FCSTD DOCUMENT  (FreeCAD 0.19R24291 (Git))
Label: v1-250-frame
License: Other
LicenseURL: GPL3
objects: Part::FeaturePython×84, Part::Feature×55, App::Part×7
note: 139 computed .brp shape members not serialized (recipe doc carries the construction recipe); baked Part::Feature solids carry a one-line shape summary decoded from their .brp

FEATURE [Part::Feature] Extrude002002003002002002002  label="380mm-tap"
  Placement = pos=(-190,0,15) rot=(0,1,0;1.5708rad)
  shape: bbox 380 x 30 x 30 mm, 95 faces (baked)
FEATURE [Part::Feature] Extrude002002003002002002007  label="380mm-tap001"
  Placement = pos=(-190,390,15) rot=(0,1,0;1.5708rad)
  shape: bbox 380 x 30 x 30 mm, 95 faces (baked)
FEATURE [Part::Feature] Extrude002002003002002002010  label="380mm-tap002"
  Placement = pos=(-190,390,535) rot=(0,1,0;1.5708rad)
  shape: bbox 380 x 30 x 30 mm, 95 faces (baked)
FEATURE [Part::Feature] Extrude002002003002002002011  label="360mm-tap"
  Placement = pos=(-205,15,535) rot=(-1,0,0;1.5708rad)
  shape: bbox 30 x 360 x 30 mm, 95 faces (baked)
FEATURE [Part::Feature] Extrude002002003002002002012  label="360mm-tap001"
  Placement = pos=(205,15,535) rot=(-1,0,0;1.5708rad)
  shape: bbox 30 x 360 x 30 mm, 95 faces (baked)
FEATURE [Part::Feature] Extrude002002003002002002013  label="380mm-tap003"
  Placement = pos=(-190,0,535) rot=(0,1,0;1.5708rad)
  shape: bbox 380 x 30 x 30 mm, 95 faces (baked)
FEATURE [Part::Feature] Extrude002002003002002002015  label="330mm-tap"
  Placement = pos=(-205,250,30) rot=(0,0,1;0rad)
  shape: bbox 30 x 30 x 330 mm, 95 faces (baked)
FEATURE [Part::Feature] Extrude002002003002002002016  label="330mm-tap001"
  Placement = pos=(205,140,30) rot=(0,0,1;0rad)
  shape: bbox 30 x 30 x 330 mm, 95 faces (baked)
FEATURE [Part::Feature] Extrude002002003002002002019  label="380mm-tap004"
  Placement = pos=(-190,390,340) rot=(0,1,0;1.5708rad)
  shape: bbox 380 x 30 x 30 mm, 95 faces (baked)
FEATURE [Part::Feature] Cut001  label="550mm-drint--tap-front-vetical"
  Placement = pos=(-205,0,0) rot=(0,0,1;0rad)
  shape: bbox 30 x 30 x 550 mm, 167 faces (baked)
FEATURE [Part::Feature] Cut002  label="550mm-drint--tap-front-vetical001"
  Placement = pos=(205,0,0) rot=(0,0,1;0rad)
  shape: bbox 30 x 30 x 550 mm, 167 faces (baked)
FEATURE [Part::Feature] Cut001001  label="550mm-drill-tap-back-vertical"
  Placement = pos=(205,390,0) rot=(0,0,1;0rad)
  shape: bbox 30 x 30 x 550 mm, 181 faces (baked)
FEATURE [Part::Feature] Cut001002  label="550mm-drill-tap-back-vertical001"
  Placement = pos=(-205,390,0) rot=(0,0,1;0rad)
  shape: bbox 30 x 30 x 550 mm, 181 faces (baked)
FEATURE [Part::Feature] Cut001003  label="330-drill-vertical"
  Placement = pos=(-205,30,30) rot=(0,0,1;0rad)
  shape: bbox 30 x 30 x 330 mm, 137 faces (baked)
FEATURE [Part::Feature] Cut001004  label="360mm-drill-tap-left-horizontal"
  Placement = pos=(-205,15,15) rot=(-1,0,0;1.5708rad)
  shape: bbox 30 x 360 x 30 mm, 109 faces (baked)
FEATURE [Part::Feature] Cut001005  label="360mm-drill-tap-right-horizontal"
  Placement = pos=(205,15,15) rot=(-1,0,0;1.5708rad)
  shape: bbox 30 x 360 x 30 mm, 109 faces (baked)
FEATURE [Part::Feature] Cut001006  label="360mm-drill-tap-left-horizontal001"
  Placement = pos=(-205,15,375) rot=(-1,0,0;1.5708rad)
  shape: bbox 30 x 360 x 30 mm, 109 faces (baked)
FEATURE [Part::Feature] Cut001007  label="360mm-drill-tap-right-horizontal001"
  Placement = pos=(205,15,375) rot=(-1,0,0;1.5708rad)
  shape: bbox 30 x 360 x 30 mm, 109 faces (baked)
FEATURE [App::Part] Part  label="250-frame"
  Group = -> [Extrude002002003002002002002,Extrude002002003002002002007,Extrude002002003002002002010,Extrude002002003002002002011,Extrude002002003002002002012,Extrude002002003002002002013,Extrude002002003002002002015,Extrude002002003002002002016,Extrude002002003002002002019,Cut001,Cut002,Cut001001,Cut001002,Cut001003,Cut001004,Cut001005,Cut001006,Cut001007]
  Origin = -> Origin
FEATURE [Part::FeaturePython] Screw039  label="M3x6-Screw048"  # Fasteners workbench fastener (typed FeaturePython)
  Placement = pos=(111,-6.5,2.5) rot=(0,0,1;0rad)
  baseObject = -> Chamfer004001 [Edge92]
  diameter = 1
  invert = false
  length = 0
  lengthCustom = 6
  matchOuter = true
  offset = 0
  thread = false
  type = 40
FEATURE [Part::Feature] Pocket003005  label="panel-mounter_D001"
  Placement = pos=(-179.5,-180,-10) rot=(0.57735,0.57735,0.57735;2.0944rad)
  shape: bbox 10 x 15 x 20 mm, 54 faces (baked)
FEATURE [Part::FeaturePython] Screw002  label="M6x12-Screw006"  # Fasteners workbench fastener (typed FeaturePython)
  Placement = pos=(55,175,-10) rot=(1,0,0;1.5708rad)
  baseObject = -> Chamfer003004004 [Edge49]
  diameter = 4
  invert = true
  length = 1
  lengthCustom = 12
  matchOuter = true
  offset = 0
  thread = false
  type = 40
FEATURE [Part::FeaturePython] HeatSet030  label="M3x4-HeatSet039"  # WARN: FeaturePython — macro-defined, semantics opaque (R4)
  Placement = pos=(-62,-7,5) rot=(0,0,1;0rad)
  diameter = 2
  invert = false
  offset = 0
FEATURE [Part::FeaturePython] HeatSet031  label="M3x4-HeatSet040"  # WARN: FeaturePython — macro-defined, semantics opaque (R4)
  Placement = pos=(-70,-144,5) rot=(0,0,1;0rad)
  diameter = 2
  invert = false
  offset = 0
FEATURE [Part::FeaturePython] HeatSet032  label="M3x4-HeatSet041"  # WARN: FeaturePython — macro-defined, semantics opaque (R4)
  Placement = pos=(-62,7,5) rot=(0,0,1;0rad)
  diameter = 2
  invert = false
  offset = 0
FEATURE [Part::FeaturePython] HeatSet033  label="M3x4-HeatSet042"  # WARN: FeaturePython — macro-defined, semantics opaque (R4)
  Placement = pos=(62,-7,5) rot=(0,0,1;0rad)
  diameter = 2
  invert = false
  offset = 0
FEATURE [Part::FeaturePython] HeatSet034  label="M3x4-HeatSet043"  # WARN: FeaturePython — macro-defined, semantics opaque (R4)
  Placement = pos=(70,-144,5) rot=(0,0,1;0rad)
  diameter = 2
  invert = false
  offset = 0
FEATURE [Part::FeaturePython] HeatSet035  label="M3x4-HeatSet044"  # WARN: FeaturePython — macro-defined, semantics opaque (R4)
  Placement = pos=(62,7,5) rot=(0,0,1;0rad)
  diameter = 2
  invert = false
  offset = 0
FEATURE [Part::FeaturePython] Screw020  label="M3x6-Screw029"  # Fasteners workbench fastener (typed FeaturePython)
  Placement = pos=(185,50.94,2.5) rot=(0,0,1;0rad)
  diameter = 1
  invert = false
  length = 0
  lengthCustom = 6
  matchOuter = true
  offset = 0
  thread = false
  type = 40
FEATURE [Part::FeaturePython] Screw021  label="M3x6-Screw030"  # Fasteners workbench fastener (typed FeaturePython)
  Placement = pos=(184,175,2.5) rot=(0,0,1;0rad)
  diameter = 1
  invert = false
  length = 0
  lengthCustom = 6
  matchOuter = true
  offset = 0
  thread = false
  type = 40
FEATURE [Part::FeaturePython] HeatSet011  label="M3x4-HeatSet013"  # WARN: FeaturePython — macro-defined, semantics opaque (R4)
  Placement = pos=(-185,-59.4,1.2e-14) rot=(0,0,1;0rad)
  baseObject = -> Pocket003020 [Edge44]
  diameter = 2
  invert = false
  offset = 0
FEATURE [Part::FeaturePython] HeatSet012  label="M3x4-HeatSet012"  # WARN: FeaturePython — macro-defined, semantics opaque (R4)
  Placement = pos=(-174.5,-175,3.91e-14) rot=(0,0,1;0rad)
  baseObject = -> Pocket003005 [Edge44]
  diameter = 2
  invert = false
  offset = 0
FEATURE [Part::FeaturePython] HeatSet013  label="M3x4-HeatSet011"  # WARN: FeaturePython — macro-defined, semantics opaque (R4)
  Placement = pos=(-82,-175,3.91e-14) rot=(0,0,1;0rad)
  baseObject = -> Pocket003006 [Edge44]
  diameter = 2
  invert = false
  offset = 0
FEATURE [Part::FeaturePython] HeatSet014  label="M3x4-HeatSet027"  # WARN: FeaturePython — macro-defined, semantics opaque (R4)
  Placement = pos=(-28,-175,3.91e-14) rot=(0,0,1;0rad)
  baseObject = -> Pocket003007 [Edge44]
  diameter = 2
  invert = false
  offset = 0
FEATURE [Part::FeaturePython] HeatSet015  label="M3x4-HeatSet020"  # WARN: FeaturePython — macro-defined, semantics opaque (R4)
  Placement = pos=(28,-175,3.91e-14) rot=(0,0,1;0rad)
  baseObject = -> Pocket003008 [Edge44]
  diameter = 2
  invert = false
  offset = 0
FEATURE [Part::FeaturePython] HeatSet016  label="M3x4-HeatSet021"  # WARN: FeaturePython — macro-defined, semantics opaque (R4)
  Placement = pos=(82,-175,3.91e-14) rot=(0,0,1;0rad)
  baseObject = -> Pocket003009 [Edge44]
  diameter = 2
  invert = false
  offset = 0
FEATURE [Part::Feature] Chamfer003004005  label="bottom-din-holder003"
  Placement = pos=(-55,165,-25) rot=(0,0,1;0rad)
  shape: bbox 40 x 31 x 21 mm, 75 faces (baked)
FEATURE [Part::Feature] Pocket003021  label="panel-mounter_R001"
  Placement = pos=(190,45.9,-10) rot=(0,0.707107,0.707107;3.14159rad)
  shape: bbox 15 x 10 x 20 mm, 54 faces (baked)
FEATURE [Part::Feature] Pocket003014  label="panel-mounter_U004"
  Placement = pos=(33,180,-10) rot=(0.57735,-0.57735,-0.57735;2.0944rad)
  shape: bbox 10 x 15 x 20 mm, 54 faces (baked)
FEATURE [Part::FeaturePython] Nut002  label="M4-Nut005"  # Fasteners workbench fastener (typed FeaturePython)
  Placement = pos=(55,161,-18) rot=(1,0,0;3.14159rad)
  baseObject = -> Chamfer003004004 [Edge141]
  diameter = 6
  invert = true
  matchOuter = true
  offset = 0
  thread = false
  type = 7
FEATURE [Part::FeaturePython] Nut003  label="M4-Nut006"  # Fasteners workbench fastener (typed FeaturePython)
  Placement = pos=(-55,161,-18) rot=(1,0,0;3.14159rad)
  baseObject = -> Chamfer003004005 [Edge141]
  diameter = 6
  invert = true
  matchOuter = true
  offset = 0
  thread = false
  type = 7
FEATURE [Part::FeaturePython] Screw012  label="M3x6-Screw004"  # Fasteners workbench fastener (typed FeaturePython)
  Placement = pos=(62,7,8) rot=(0,0,1;0rad)
  baseObject = -> Cut002015026005020007004002 [Edge40]
  diameter = 1
  invert = false
  length = 0
  lengthCustom = 6
  matchOuter = true
  offset = 0
  thread = false
  type = 40
FEATURE [Part::FeaturePython] Screw013  label="M3x6-Screw005"  # Fasteners workbench fastener (typed FeaturePython)
  Placement = pos=(62,-7,8) rot=(0,0,1;0rad)
  baseObject = -> Cut002015026005020007004002 [Edge39]
  diameter = 1
  invert = false
  length = 0
  lengthCustom = 6
  matchOuter = true
  offset = 0
  thread = false
  type = 40
FEATURE [Part::FeaturePython] Screw014  label="M3x6-Screw006"  # Fasteners workbench fastener (typed FeaturePython)
  Placement = pos=(48,-7,8) rot=(0,0,1;0rad)
  baseObject = -> Cut002015026005020007004002 [Edge41]
  diameter = 1
  invert = false
  length = 0
  lengthCustom = 6
  matchOuter = true
  offset = 0
  thread = false
  type = 40
FEATURE [Part::FeaturePython] Screw  label="M6x12-Screw004"  # Fasteners workbench fastener (typed FeaturePython)
  Placement = pos=(-55,-175,-10) rot=(-1,0,0;1.5708rad)
  baseObject = -> Chamfer003004002 [Edge49]
  diameter = 4
  invert = true
  length = 1
  lengthCustom = 12
  matchOuter = true
  offset = 0
  thread = false
  type = 40
FEATURE [Part::FeaturePython] Screw015  label="M3x6-Screw007"  # Fasteners workbench fastener (typed FeaturePython)
  Placement = pos=(48,7,8) rot=(0,0,1;0rad)
  baseObject = -> Cut002015026005020007004002 [Edge42]
  diameter = 1
  invert = false
  length = 0
  lengthCustom = 6
  matchOuter = true
  offset = 0
  thread = false
  type = 40
FEATURE [Part::FeaturePython] Screw016  label="M3x6-Screw008"  # Fasteners workbench fastener (typed FeaturePython)
  Placement = pos=(-48,7,8) rot=(0,0,1;0rad)
  baseObject = -> Cut002015026005020007004001 [Edge40]
  diameter = 1
  invert = false
  length = 0
  lengthCustom = 6
  matchOuter = true
  offset = 0
  thread = false
  type = 40
FEATURE [Part::FeaturePython] Screw017  label="M3x6-Screw009"  # Fasteners workbench fastener (typed FeaturePython)
  Placement = pos=(-48,-7,8) rot=(0,0,1;0rad)
  baseObject = -> Cut002015026005020007004001 [Edge39]
  diameter = 1
  invert = false
  length = 0
  lengthCustom = 6
  matchOuter = true
  offset = 0
  thread = false
  type = 40
FEATURE [Part::FeaturePython] Screw018  label="M3x6-Screw010"  # Fasteners workbench fastener (typed FeaturePython)
  Placement = pos=(-62,-7,8) rot=(0,0,1;0rad)
  baseObject = -> Cut002015026005020007004001 [Edge41]
  diameter = 1
  invert = false
  length = 0
  lengthCustom = 6
  matchOuter = true
  offset = 0
  thread = false
  type = 40
FEATURE [Part::FeaturePython] Screw019  label="M3x6-Screw011"  # Fasteners workbench fastener (typed FeaturePython)
  Placement = pos=(-62,7,8) rot=(0,0,1;0rad)
  baseObject = -> Cut002015026005020007004001 [Edge42]
  diameter = 1
  invert = false
  length = 0
  lengthCustom = 6
  matchOuter = true
  offset = 0
  thread = false
  type = 40
FEATURE [Part::Feature] Pocket003007  label="panel-mounter_D003"
  Placement = pos=(-33,-180,-10) rot=(0.57735,0.57735,0.57735;2.0944rad)
  shape: bbox 10 x 15 x 20 mm, 54 faces (baked)
FEATURE [Part::Feature] Pocket003006  label="panel-mounter_D002"
  Placement = pos=(-87,-180,-10) rot=(0.57735,0.57735,0.57735;2.0944rad)
  shape: bbox 10 x 15 x 20 mm, 54 faces (baked)
FEATURE [Part::Feature] Chamfer005007002029002004001  label="back-din-cap"
  Placement = pos=(-55,165,-25) rot=(0,0,1;0rad)
  shape: bbox 40 x 30 x 6 mm, 55 faces (baked)
FEATURE [Part::FeaturePython] Screw004  label="M4x25-Screw"  # Fasteners workbench fastener (typed FeaturePython)
  Placement = pos=(-55,161,2.5) rot=(0,0,1;0rad)
  baseObject = -> Chamfer005007002029002004001 [Edge49]
  diameter = 2
  invert = false
  length = 7
  lengthCustom = 25
  matchOuter = true
  offset = 0
  thread = false
  type = 40
FEATURE [Part::FeaturePython] HeatSet002  label="M3x4-HeatSet025"  # WARN: FeaturePython — macro-defined, semantics opaque (R4)
  Placement = pos=(184,175,1.8e-15) rot=(0,0,1;0rad)
  baseObject = -> Pocket003016 [Edge44]
  diameter = 2
  invert = false
  offset = 0
FEATURE [Part::FeaturePython] HeatSet003  label="M3x4-HeatSet026"  # WARN: FeaturePython — macro-defined, semantics opaque (R4)
  Placement = pos=(82,175,1.8e-15) rot=(0,0,1;0rad)
  baseObject = -> Pocket003015 [Edge44]
  diameter = 2
  invert = false
  offset = 0
FEATURE [Part::FeaturePython] HeatSet004  label="M3x4-HeatSet024"  # WARN: FeaturePython — macro-defined, semantics opaque (R4)
  Placement = pos=(28,175,1.8e-15) rot=(0,0,1;0rad)
  baseObject = -> Pocket003014 [Edge44]
  diameter = 2
  invert = false
  offset = 0
FEATURE [Part::FeaturePython] HeatSet005  label="M3x4-HeatSet028"  # WARN: FeaturePython — macro-defined, semantics opaque (R4)
  Placement = pos=(-28,175,1.8e-15) rot=(0,0,1;0rad)
  baseObject = -> Pocket003013 [Edge44]
  diameter = 2
  invert = false
  offset = 0
FEATURE [Part::FeaturePython] HeatSet006  label="M3x4-HeatSet018"  # WARN: FeaturePython — macro-defined, semantics opaque (R4)
  Placement = pos=(-82,175,1.8e-15) rot=(0,0,1;0rad)
  baseObject = -> Pocket003012 [Edge44]
  diameter = 2
  invert = false
  offset = 0
FEATURE [Part::FeaturePython] HeatSet007  label="M3x4-HeatSet017"  # WARN: FeaturePython — macro-defined, semantics opaque (R4)
  Placement = pos=(-184,175,1.8e-15) rot=(0,0,1;0rad)
  baseObject = -> Pocket003011 [Edge44]
  diameter = 2
  invert = false
  offset = 0
FEATURE [Part::FeaturePython] HeatSet008  label="M3x4-HeatSet016"  # WARN: FeaturePython — macro-defined, semantics opaque (R4)
  Placement = pos=(-185,32.4,-7.1e-15) rot=(0,0,1;0rad)
  baseObject = -> Pocket003017 [Edge44]
  diameter = 2
  invert = false
  offset = 0
FEATURE [Part::FeaturePython] HeatSet009  label="M3x4-HeatSet023"  # WARN: FeaturePython — macro-defined, semantics opaque (R4)
  Placement = pos=(-185,6.6,-1.8e-15) rot=(0,0,1;0rad)
  baseObject = -> Pocket003018 [Edge44]
  diameter = 2
  invert = false
  offset = 0
FEATURE [Part::FeaturePython] HeatSet010  label="M3x4-HeatSet014"  # WARN: FeaturePython — macro-defined, semantics opaque (R4)
  Placement = pos=(-185,-6.5,2e-15) rot=(0,0,1;0rad)
  baseObject = -> Pocket003019 [Edge44]
  diameter = 2
  invert = false
  offset = 0
FEATURE [Part::Feature] Cut002015026005020007004003  label="front-din-cap001"
  Placement = pos=(55,-165,0) rot=(0,0,1;0rad)
  shape: bbox 40 x 41.5 x 9 mm, 50 faces (baked)
FEATURE [Part::FeaturePython] Screw022  label="M3x6-Screw031"  # Fasteners workbench fastener (typed FeaturePython)
  Placement = pos=(82,175,2.5) rot=(0,0,1;0rad)
  diameter = 1
  invert = false
  length = 0
  lengthCustom = 6
  matchOuter = true
  offset = 0
  thread = false
  type = 40
FEATURE [Part::FeaturePython] Screw023  label="M3x6-Screw032"  # Fasteners workbench fastener (typed FeaturePython)
  Placement = pos=(28,175,2.5) rot=(0,0,1;0rad)
  diameter = 1
  invert = false
  length = 0
  lengthCustom = 6
  matchOuter = true
  offset = 0
  thread = false
  type = 40
FEATURE [Part::FeaturePython] Screw024  label="M3x6-Screw033"  # Fasteners workbench fastener (typed FeaturePython)
  Placement = pos=(-28,175,2.5) rot=(0,0,1;0rad)
  diameter = 1
  invert = false
  length = 0
  lengthCustom = 6
  matchOuter = true
  offset = 0
  thread = false
  type = 40
FEATURE [Part::FeaturePython] Screw025  label="M3x6-Screw034"  # Fasteners workbench fastener (typed FeaturePython)
  Placement = pos=(-82,175,2.5) rot=(0,0,1;0rad)
  diameter = 1
  invert = false
  length = 0
  lengthCustom = 6
  matchOuter = true
  offset = 0
  thread = false
  type = 40
FEATURE [Part::FeaturePython] Screw026  label="M3x6-Screw035"  # Fasteners workbench fastener (typed FeaturePython)
  Placement = pos=(-184,175,2.5) rot=(0,0,1;0rad)
  diameter = 1
  invert = false
  length = 0
  lengthCustom = 6
  matchOuter = true
  offset = 0
  thread = false
  type = 40
FEATURE [Part::FeaturePython] Screw027  label="M3x6-Screw036"  # Fasteners workbench fastener (typed FeaturePython)
  Placement = pos=(-185,32.5,2.5) rot=(0,0,1;0rad)
  diameter = 1
  invert = false
  length = 0
  lengthCustom = 6
  matchOuter = true
  offset = 0
  thread = false
  type = 40
FEATURE [Part::FeaturePython] Screw028  label="M3x6-Screw042"  # Fasteners workbench fastener (typed FeaturePython)
  Placement = pos=(-185,-6.5,2.5) rot=(0,0,1;0rad)
  diameter = 1
  invert = false
  length = 0
  lengthCustom = 6
  matchOuter = true
  offset = 0
  thread = false
  type = 40
FEATURE [Part::Feature] Cut002015026005020007004001  label="center-panel-connector"
  Placement = pos=(-55,0,5) rot=(0,0,1;0rad)
  shape: bbox 22 x 22 x 3 mm, 24 faces (baked)
FEATURE [Part::FeaturePython] Screw001  label="M6x12-Screw005"  # Fasteners workbench fastener (typed FeaturePython)
  Placement = pos=(55,-175,-10) rot=(-1,0,0;1.5708rad)
  baseObject = -> Chamfer003004003 [Edge49]
  diameter = 4
  invert = true
  length = 1
  lengthCustom = 12
  matchOuter = true
  offset = 0
  thread = false
  type = 40
FEATURE [Part::Feature] Pocket003008  label="panel-mounter_D004"
  Placement = pos=(23,-180,-10) rot=(0.57735,0.57735,0.57735;2.0944rad)
  shape: bbox 10 x 15 x 20 mm, 54 faces (baked)
FEATURE [Part::FeaturePython] Screw029  label="M3x6-Screw043"  # Fasteners workbench fastener (typed FeaturePython)
  Placement = pos=(-185,-59.36,2.5) rot=(0,0,1;0rad)
  diameter = 1
  invert = false
  length = 0
  lengthCustom = 6
  matchOuter = true
  offset = 0
  thread = false
  type = 40
FEATURE [Part::FeaturePython] Screw030  label="M3x6-Screw044"  # Fasteners workbench fastener (typed FeaturePython)
  Placement = pos=(-174.5,-175,2.5) rot=(0,0,1;0rad)
  diameter = 1
  invert = false
  length = 0
  lengthCustom = 6
  matchOuter = true
  offset = 0
  thread = false
  type = 40
FEATURE [Part::FeaturePython] Screw031  label="M3x6-Screw045"  # Fasteners workbench fastener (typed FeaturePython)
  Placement = pos=(-82,-175,2.5) rot=(0,0,1;0rad)
  diameter = 1
  invert = false
  length = 0
  lengthCustom = 6
  matchOuter = true
  offset = 0
  thread = false
  type = 40
FEATURE [Part::FeaturePython] Screw032  label="M3x6-Screw040"  # Fasteners workbench fastener (typed FeaturePython)
  Placement = pos=(28,-175,2.5) rot=(0,0,1;0rad)
  diameter = 1
  invert = false
  length = 0
  lengthCustom = 6
  matchOuter = true
  offset = 0
  thread = false
  type = 40
FEATURE [Part::FeaturePython] Screw033  label="M3x6-Screw041"  # Fasteners workbench fastener (typed FeaturePython)
  Placement = pos=(-28,-175,2.5) rot=(0,0,1;0rad)
  diameter = 1
  invert = false
  length = 0
  lengthCustom = 6
  matchOuter = true
  offset = 0
  thread = false
  type = 40
FEATURE [Part::FeaturePython] Screw034  label="M3x6-Screw037"  # Fasteners workbench fastener (typed FeaturePython)
  Placement = pos=(184,-175,2.5) rot=(0,0,1;0rad)
  diameter = 1
  invert = false
  length = 0
  lengthCustom = 6
  matchOuter = true
  offset = 0
  thread = false
  type = 40
FEATURE [Part::FeaturePython] Screw035  label="M3x6-Screw038"  # Fasteners workbench fastener (typed FeaturePython)
  Placement = pos=(82,-175,2.5) rot=(0,0,1;0rad)
  diameter = 1
  invert = false
  length = 0
  lengthCustom = 6
  matchOuter = true
  offset = 0
  thread = false
  type = 40
FEATURE [Part::FeaturePython] Screw036  label="M3x6-Screw039"  # Fasteners workbench fastener (typed FeaturePython)
  Placement = pos=(185,-77.5,2.5) rot=(0,0,1;0rad)
  diameter = 1
  invert = false
  length = 0
  lengthCustom = 6
  matchOuter = true
  offset = 0
  thread = false
  type = 40
FEATURE [Part::Feature] Common001003002002003003  label="din-rail-332mm002"
  Placement = pos=(93,53,20) rot=(0.707107,-0.707107,0;3.14159rad)
  shape: bbox 35 x 332 x 7.5 mm, 70 faces (baked)
FEATURE [Part::Feature] Pocket003019  label="panel-mounter_L003"
  Placement = pos=(-190,-1.5,-10) rot=(1,0,0;1.5708rad)
  shape: bbox 15 x 10 x 20 mm, 54 faces (baked)
FEATURE [Part::Feature] Pocket003017  label="panel-mounter_L001"
  Placement = pos=(-190,37.4,-10) rot=(1,0,0;1.5708rad)
  shape: bbox 15 x 10 x 20 mm, 54 faces (baked)
FEATURE [Part::FeaturePython] Screw010  label="M3x6-Screw002"  # Fasteners workbench fastener (typed FeaturePython)
  Placement = pos=(-40,-144,8) rot=(0,0,1;0rad)
  baseObject = -> Cut002015026005020007004004 [Edge45]
  diameter = 1
  invert = false
  length = 0
  lengthCustom = 6
  matchOuter = true
  offset = 0
  thread = false
  type = 40
FEATURE [Part::FeaturePython] Screw011  label="M3x6-Screw003"  # Fasteners workbench fastener (typed FeaturePython)
  Placement = pos=(-70,-144,8) rot=(0,0,1;0rad)
  baseObject = -> Cut002015026005020007004004 [Edge44]
  diameter = 1
  invert = false
  length = 0
  lengthCustom = 6
  matchOuter = true
  offset = 0
  thread = false
  type = 40
FEATURE [Part::Feature] Pocket003022  label="panel-mounter_R002"
  Placement = pos=(190,-82.5,-10) rot=(0,0.707107,0.707107;3.14159rad)
  shape: bbox 15 x 10 x 20 mm, 54 faces (baked)
FEATURE [Part::Feature] Chamfer003004004  label="bottom-din-holder002"
  Placement = pos=(55,165,-25) rot=(0,0,1;0rad)
  shape: bbox 40 x 31 x 21 mm, 75 faces (baked)
FEATURE [Part::Feature] Pocket003009  label="panel-mounter_D005"
  Placement = pos=(77,-180,-10) rot=(0.57735,0.57735,0.57735;2.0944rad)
  shape: bbox 10 x 15 x 20 mm, 54 faces (baked)
FEATURE [Part::Feature] Cut002015026005020007004002  label="center-panel-connector001"
  Placement = pos=(55,0,5) rot=(0,0,1;0rad)
  shape: bbox 22 x 22 x 3 mm, 24 faces (baked)
FEATURE [Part::Feature] Pocket003012  label="panel-mounter_U002"
  Placement = pos=(-77,180,-10) rot=(0.57735,-0.57735,-0.57735;2.0944rad)
  shape: bbox 10 x 15 x 20 mm, 54 faces (baked)
FEATURE [Part::FeaturePython] Screw003  label="M6x12-Screw"  # Fasteners workbench fastener (typed FeaturePython)
  Placement = pos=(-55,175,-10) rot=(1,0,0;1.5708rad)
  baseObject = -> Chamfer003004005 [Edge49]
  diameter = 4
  invert = true
  length = 1
  lengthCustom = 12
  matchOuter = true
  offset = 0
  thread = false
  type = 40
FEATURE [Part::FeaturePython] Nut  label="M4-Nut"  # Fasteners workbench fastener (typed FeaturePython)
  Placement = pos=(-55,-161,-18) rot=(1,0,0;3.14159rad)
  baseObject = -> Chamfer003004002 [Edge141]
  diameter = 6
  invert = true
  matchOuter = true
  offset = 0
  thread = false
  type = 7
FEATURE [Part::Feature] Pocket003011  label="panel-mounter_U001"
  Placement = pos=(-179,180,-10) rot=(0.57735,-0.57735,-0.57735;2.0944rad)
  shape: bbox 10 x 15 x 20 mm, 54 faces (baked)
FEATURE [Part::FeaturePython] HeatSet  label="M3x4-HeatSet"  # WARN: FeaturePython — macro-defined, semantics opaque (R4)
  Placement = pos=(70,170,5) rot=(0,0,1;0rad)
  baseObject = -> Chamfer005007002029002004002 [Edge114]
  diameter = 2
  invert = false
  offset = 0
FEATURE [Part::FeaturePython] HeatSet001  label="M3x4-HeatSet001"  # WARN: FeaturePython — macro-defined, semantics opaque (R4)
  Placement = pos=(40,170,5) rot=(0,0,1;0rad)
  baseObject = -> Chamfer005007002029002004002 [Edge88]
  diameter = 2
  invert = false
  offset = 0
FEATURE [Part::FeaturePython] Screw005  label="M4x25-Screw001"  # Fasteners workbench fastener (typed FeaturePython)
  Placement = pos=(55,161,2.5) rot=(0,0,1;0rad)
  baseObject = -> Chamfer005007002029002004002 [Edge49]
  diameter = 2
  invert = false
  length = 7
  lengthCustom = 25
  matchOuter = true
  offset = 0
  thread = false
  type = 40
FEATURE [Part::FeaturePython] Screw006  label="M4x25-Screw002"  # Fasteners workbench fastener (typed FeaturePython)
  Placement = pos=(55,-161,2.5) rot=(0,0,1;0rad)
  baseObject = -> Cut002015026005020007004003 [Edge118]
  diameter = 2
  invert = false
  length = 7
  lengthCustom = 25
  matchOuter = true
  offset = 0
  thread = false
  type = 40
FEATURE [Part::Feature] Chamfer005007002029002004002  label="back-din-cap001"
  Placement = pos=(55,165,-25) rot=(0,0,1;0rad)
  shape: bbox 40 x 30 x 6 mm, 55 faces (baked)
FEATURE [Part::Feature] Common001003002002003002  label="din-rail-332mm001"
  Placement = pos=(-17,53,20) rot=(0.707107,-0.707107,0;3.14159rad)
  shape: bbox 35 x 332 x 7.5 mm, 70 faces (baked)
FEATURE [Part::Feature] Chamfer003004003  label="bottom-din-holder001"
  Placement = pos=(55,-165,-25) rot=(0,0,1;3.14159rad)
  shape: bbox 40 x 31 x 21 mm, 75 faces (baked)
FEATURE [Part::Feature] Pocket003015  label="panel-mounter_U005"
  Placement = pos=(87,180,-10) rot=(0.57735,-0.57735,-0.57735;2.0944rad)
  shape: bbox 10 x 15 x 20 mm, 54 faces (baked)
FEATURE [Part::Feature] Cut002015026005020007004004  label="front-din-cap"
  Placement = pos=(-55,-165,0) rot=(0,0,1;0rad)
  shape: bbox 40 x 41.5 x 9 mm, 50 faces (baked)
FEATURE [Part::FeaturePython] Nut001  label="M4-Nut004"  # Fasteners workbench fastener (typed FeaturePython)
  Placement = pos=(55,-161,-18) rot=(1,0,0;3.14159rad)
  baseObject = -> Chamfer003004003 [Edge141]
  diameter = 6
  invert = true
  matchOuter = true
  offset = 0
  thread = false
  type = 7
FEATURE [Part::Feature] Pocket003016  label="panel-mounter_U006"
  Placement = pos=(189,180,-10) rot=(0.57735,-0.57735,-0.57735;2.0944rad)
  shape: bbox 10 x 15 x 20 mm, 54 faces (baked)
FEATURE [Part::FeaturePython] Screw007  label="M4x25-Screw003"  # Fasteners workbench fastener (typed FeaturePython)
  Placement = pos=(-55,-161,2.5) rot=(0,0,1;0rad)
  baseObject = -> Cut002015026005020007004004 [Edge118]
  diameter = 2
  invert = false
  length = 7
  lengthCustom = 25
  matchOuter = true
  offset = 0
  thread = false
  type = 40
FEATURE [Part::FeaturePython] Screw008  label="M3x6-Screw"  # Fasteners workbench fastener (typed FeaturePython)
  Placement = pos=(70,-144,8) rot=(0,0,1;0rad)
  baseObject = -> Cut002015026005020007004003 [Edge45]
  diameter = 1
  invert = false
  length = 0
  lengthCustom = 6
  matchOuter = true
  offset = 0
  thread = false
  type = 40
FEATURE [Part::FeaturePython] Screw009  label="M3x6-Screw001"  # Fasteners workbench fastener (typed FeaturePython)
  Placement = pos=(40,-144,8) rot=(0,0,1;0rad)
  baseObject = -> Cut002015026005020007004003 [Edge44]
  diameter = 1
  invert = false
  length = 0
  lengthCustom = 6
  matchOuter = true
  offset = 0
  thread = false
  type = 40
FEATURE [Part::Feature] Pocket003020  label="panel-mounter_L004"
  Placement = pos=(-190,-54.4,-10) rot=(1,0,0;1.5708rad)
  shape: bbox 15 x 10 x 20 mm, 54 faces (baked)
FEATURE [Part::Feature] Pocket003010  label="panel-mounter_D006"
  Placement = pos=(179,-180,-10) rot=(0.57735,0.57735,0.57735;2.0944rad)
  shape: bbox 10 x 15 x 20 mm, 54 faces (baked)
FEATURE [Part::Feature] Pocket003018  label="panel-mounter_L002"
  Placement = pos=(-190,11.6,-10) rot=(1,0,0;1.5708rad)
  shape: bbox 15 x 10 x 20 mm, 54 faces (baked)
FEATURE [Part::Feature] Pocket003013  label="panel-mounter_U003"
  Placement = pos=(-23,180,-10) rot=(0.57735,-0.57735,-0.57735;2.0944rad)
  shape: bbox 10 x 15 x 20 mm, 54 faces (baked)
FEATURE [Part::FeaturePython] HeatSet023  label="M3x4-HeatSet032"  # WARN: FeaturePython — macro-defined, semantics opaque (R4)
  Placement = pos=(-15,143,5) rot=(0,0,1;0rad)
  diameter = 2
  invert = false
  offset = 0
FEATURE [Part::FeaturePython] HeatSet024  label="M3x4-HeatSet033"  # WARN: FeaturePython — macro-defined, semantics opaque (R4)
  Placement = pos=(-48,7,5) rot=(0,0,1;0rad)
  diameter = 2
  invert = false
  offset = 0
FEATURE [Part::FeaturePython] HeatSet025  label="M3x4-HeatSet034"  # WARN: FeaturePython — macro-defined, semantics opaque (R4)
  Placement = pos=(48,7,5) rot=(0,0,1;0rad)
  diameter = 2
  invert = false
  offset = 0
FEATURE [Part::FeaturePython] HeatSet026  label="M3x4-HeatSet035"  # WARN: FeaturePython — macro-defined, semantics opaque (R4)
  Placement = pos=(-48,-7,5) rot=(0,0,1;0rad)
  diameter = 2
  invert = false
  offset = 0
FEATURE [Part::FeaturePython] HeatSet027  label="M3x4-HeatSet036"  # WARN: FeaturePython — macro-defined, semantics opaque (R4)
  Placement = pos=(48,-7,5) rot=(0,0,1;0rad)
  diameter = 2
  invert = false
  offset = 0
FEATURE [Part::FeaturePython] HeatSet028  label="M3x4-HeatSet037"  # WARN: FeaturePython — macro-defined, semantics opaque (R4)
  Placement = pos=(40,-144,5) rot=(0,0,1;0rad)
  diameter = 2
  invert = false
  offset = 0
FEATURE [Part::FeaturePython] HeatSet029  label="M3x4-HeatSet038"  # WARN: FeaturePython — macro-defined, semantics opaque (R4)
  Placement = pos=(-40,-144,5) rot=(0,0,1;0rad)
  diameter = 2
  invert = false
  offset = 0
FEATURE [Part::FeaturePython] HeatSet017  label="M3x4-HeatSet022"  # WARN: FeaturePython — macro-defined, semantics opaque (R4)
  Placement = pos=(184,-175,3.91e-14) rot=(0,0,1;0rad)
  baseObject = -> Pocket003010 [Edge44]
  diameter = 2
  invert = false
  offset = 0
FEATURE [Part::FeaturePython] HeatSet018  label="M3x4-HeatSet019"  # WARN: FeaturePython — macro-defined, semantics opaque (R4)
  Placement = pos=(185,-77.5,1.49e-14) rot=(0,0,1;0rad)
  baseObject = -> Pocket003022 [Edge44]
  diameter = 2
  invert = false
  offset = 0
FEATURE [Part::FeaturePython] HeatSet019  label="M3x4-HeatSet015"  # WARN: FeaturePython — macro-defined, semantics opaque (R4)
  Placement = pos=(185,50.9,-1.4e-14) rot=(0,0,1;0rad)
  baseObject = -> Pocket003021 [Edge44]
  diameter = 2
  invert = false
  offset = 0
FEATURE [App::Part] Part003  label="panel-mounter"
  Group = -> [Pocket003005,Pocket003006,Pocket003007,Pocket003008,Pocket003009,Pocket003010,Pocket003011,Pocket003012,Pocket003013,Pocket003014,Pocket003015,Pocket003016,Pocket003017,Pocket003018,Pocket003019,Pocket003020,Pocket003021,Pocket003022,HeatSet013,HeatSet012,HeatSet011,HeatSet010,HeatSet019,HeatSet008,HeatSet007,HeatSet006,HeatSet018,HeatSet015,HeatSet016,HeatSet017,HeatSet009,HeatSet004,HeatSet002,+3 more]
  Origin = -> Origin003
FEATURE [Part::FeaturePython] HeatSet020  label="M3x4-HeatSet029"  # WARN: FeaturePython — macro-defined, semantics opaque (R4)
  Placement = pos=(15,143,5) rot=(0,0,1;0rad)
  diameter = 2
  invert = false
  offset = 0
FEATURE [Part::FeaturePython] HeatSet021  label="M3x4-HeatSet030"  # WARN: FeaturePython — macro-defined, semantics opaque (R4)
  Placement = pos=(15,103,5) rot=(0,0,1;0rad)
  diameter = 2
  invert = false
  offset = 0
FEATURE [Part::FeaturePython] HeatSet022  label="M3x4-HeatSet031"  # WARN: FeaturePython — macro-defined, semantics opaque (R4)
  Placement = pos=(-15,103,5) rot=(0,0,1;0rad)
  diameter = 2
  invert = false
  offset = 0
FEATURE [Part::Feature] Chamfer003004002  label="bottom-din-holder"
  Placement = pos=(-55,-165,-25) rot=(0,0,1;3.14159rad)
  shape: bbox 40 x 31 x 21 mm, 75 faces (baked)
FEATURE [Part::Feature] Chamfer001001  label="panel-BL"
  shape: bbox 134 x 179 x 5 mm, 131 faces (baked)
FEATURE [Part::Feature] Chamfer007  label="panel-side-connector"
  Placement = pos=(111,0,-5) rot=(0,0,1;0rad)
  shape: bbox 10 x 23 x 5 mm, 32 faces (baked)
FEATURE [Part::Feature] Chamfer005001  label="panel-BR"
  shape: bbox 134 x 179 x 5 mm, 57 faces (baked)
FEATURE [Part::Feature] Chamfer006001  label="panel-BC"
  shape: bbox 109 x 179 x 5 mm, 52 faces (baked)
FEATURE [Part::Feature] Chamfer002001  label="panel-FL"
  shape: bbox 134 x 179 x 5 mm, 78 faces (baked)
FEATURE [Part::Feature] Chamfer003001  label="panel-FC"
  shape: bbox 109 x 179 x 5 mm, 46 faces (baked)
FEATURE [Part::Feature] Chamfer004001  label="panel-FR"
  shape: bbox 134 x 179 x 5 mm, 66 faces (baked)
FEATURE [Part::FeaturePython] HeatSet036  label="M3x4-HeatSet045"  # WARN: FeaturePython — macro-defined, semantics opaque (R4)
  Placement = pos=(111,-6.5,0) rot=(0,0,1;0rad)
  baseObject = -> Chamfer007 [Edge39]
  diameter = 2
  invert = false
  offset = 0
FEATURE [Part::FeaturePython] Screw037  label="M3x6-Screw046"  # Fasteners workbench fastener (typed FeaturePython)
  Placement = pos=(-185,6.5,2.5) rot=(0,0,1;0rad)
  baseObject = -> Chamfer001001 [Edge126]
  diameter = 1
  invert = false
  length = 0
  lengthCustom = 6
  matchOuter = true
  offset = 0
  thread = false
  type = 40
FEATURE [Part::FeaturePython] HeatSet037  label="M3-HeatSet001"  # WARN: FeaturePython — macro-defined, semantics opaque (R4)
  Placement = pos=(111,6.5,0) rot=(0,0,1;0rad)
  baseObject = -> Chamfer007 [Edge40]
  diameter = 2
  invert = false
  offset = 0
FEATURE [App::Part] Part002  label="panel-connector"
  Group = -> [Cut002015026005020007004002,Cut002015026005020007004001,Screw012,Screw013,Screw014,Screw015,Screw016,Screw017,Screw018,Screw019,Chamfer007,HeatSet036,HeatSet037]
  Origin = -> Origin002
FEATURE [Part::FeaturePython] Screw038  label="M3x6-Screw047"  # Fasteners workbench fastener (typed FeaturePython)
  Placement = pos=(111,6.5,2.5) rot=(0,0,1;0rad)
  baseObject = -> Chamfer005001 [Edge76]
  diameter = 1
  invert = false
  length = 0
  lengthCustom = 6
  matchOuter = true
  offset = 0
  thread = false
  type = 40
FEATURE [App::Part] Part001  label="panel"
  Group = -> [HeatSet020,HeatSet021,HeatSet022,HeatSet023,HeatSet024,HeatSet025,HeatSet026,HeatSet027,HeatSet028,HeatSet029,HeatSet030,HeatSet031,HeatSet032,HeatSet033,HeatSet034,HeatSet035,Screw020,Screw021,Screw022,Screw023,Screw024,Screw025,Screw026,Screw027,Screw028,Screw029,Screw030,Screw031,Screw032,Screw033,Screw034,Screw035,Screw036,Chamfer001001,Chamfer002001,Chamfer003001,Chamfer004001,Chamfer005001,+4 more]
  Origin = -> Origin001
FEATURE [Part::FeaturePython] HeatSet038  label="M3x4-HeatSet046"  # WARN: FeaturePython — macro-defined, semantics opaque (R4)
  Placement = pos=(-70,170,5) rot=(0,0,1;0rad)
  baseObject = -> Chamfer005007002029002004001 [Edge88]
  diameter = 2
  invert = false
  offset = 0
FEATURE [Part::FeaturePython] HeatSet039  label="M3x4-HeatSet002"  # WARN: FeaturePython — macro-defined, semantics opaque (R4)
  Placement = pos=(-40,170,5) rot=(0,0,1;0rad)
  baseObject = -> Chamfer005007002029002004001 [Edge114]
  diameter = 2
  invert = false
  offset = 0
FEATURE [App::Part] Part007  label="bottom-din"
  Group = -> [Common001003002002003003,Common001003002002003002,Cut002015026005020007004004,Chamfer005007002029002004001,Chamfer005007002029002004002,Cut002015026005020007004003,Chamfer003004002,Chamfer003004003,Chamfer003004004,Chamfer003004005,Screw003,Screw,Screw001,Screw002,Nut,Nut001,Nut002,Nut003,Screw004,Screw005,Screw006,Screw007,Screw008,Screw009,Screw010,Screw011,HeatSet001,HeatSet,HeatSet039,+1 more]
  Origin = -> Origin007
FEATURE [App::Part] Part004  label="bottom-panel"
  Group = -> [Part007,Part001,Part002,Part003]
  Origin = -> Origin004
  Placement = pos=(0,195.5,22) rot=(0,0,1;0rad)
FEATURE [App::Part] Part006  label="v1-250"
  Group = -> [Part,Part004]
  Origin = -> Origin006
